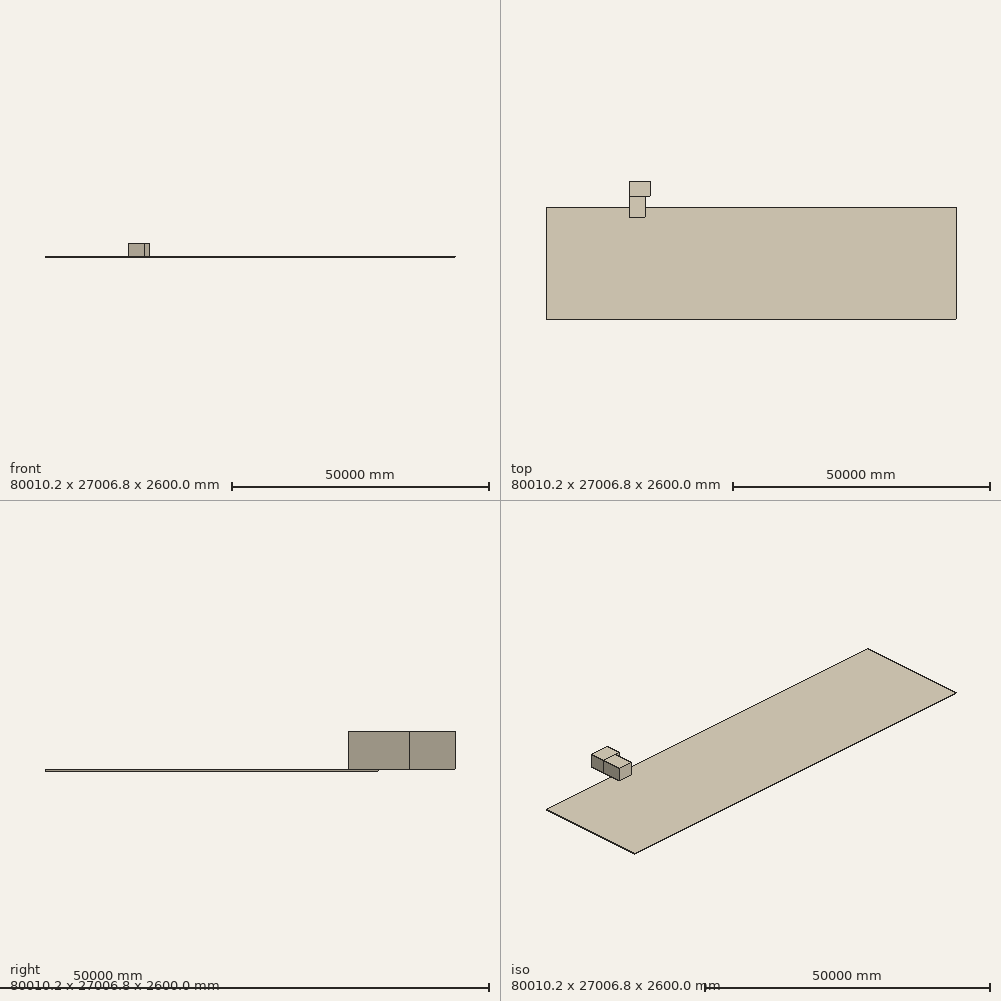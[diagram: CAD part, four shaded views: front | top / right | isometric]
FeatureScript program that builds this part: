
annotation { "Feature Type Name" : "Feature", "Feature Type Description" : "" }
export const myFeature = defineFeature(function(context is Context, id is Id, definition is map)
    precondition{}
    {
        {
            var Q0;
            Q0=qCreatedBy(makeId("Top.planeOp"),FACE);
            var sketch = newSketch(context, id + "F0", { "sketchPlane" : qUnion([Q0])});
            skLineSegment(sketch, "E0.bottom", {"start": v(-72.67, -73.64) * mm, "end": v(79937.58, -73.64) * mm});
            skLineSegment(sketch, "E0.top", {"start": v(-72.67, -21994.04) * mm, "end": v(79937.58, -21994.04) * mm});
            skLineSegment(sketch, "E0.left", {"start": v(-72.67, -73.64) * mm, "end": v(-72.67, -21994.04) * mm});
            skLineSegment(sketch, "E0.right", {"start": v(79937.58, -73.64) * mm, "end": v(79937.58, -21994.04) * mm});
            skSolve(sketch);
        }
        {
            var Q0;
            Q0 = qSketchRegion(id + "F0", true);
            extrude(context, id + "F1", {"entities" : qUnion([Q0]), "depth" : 100 * mm});
        }
        {
            var Q0;
            Q0=makeQuery(id+"F1.opExtrude","CAP_FACE",FACE,{"disambiguationData":[OSD([sQuery(id+"F0.wireOp",EDGE,"E0.bottom"),sQuery(id+"F0.wireOp",EDGE,"E0.top"),sQuery(id+"F0.wireOp",EDGE,"E0.left"),sQuery(id+"F0.wireOp",EDGE,"E0.right")])],"isStart":false});
            var sketch = newSketch(context, id + "F2", { "sketchPlane" : qUnion([Q0])});
            skLineSegment(sketch, "E1.bottom", {"start": v(16143.83, 1984.38) * mm, "end": v(20149.11, 1984.38) * mm});
            skLineSegment(sketch, "E1.top", {"start": v(16143.83, 5012.76) * mm, "end": v(20149.11, 5012.76) * mm});
            skLineSegment(sketch, "E1.left", {"start": v(16143.83, 1984.38) * mm, "end": v(16143.83, 5012.76) * mm});
            skLineSegment(sketch, "E1.right", {"start": v(20149.11, 1984.38) * mm, "end": v(20149.11, 5012.76) * mm});
            skSolve(sketch);
        }
        {
            var Q0;
            Q0=makeQuery(id+"F2.imprint","IMPRINT",FACE,{"disambiguationData":[TD([[makeQuery(id+"F2.imprint","IMPRINT",EDGE,{"derivedFrom":sQuery(id+"F2.wireOp",EDGE,"E1.bottom")}),1.0]])]});
            extrude(context, id + "F3", {"entities" : qUnion([Q0]), "depth" : 2500 * mm});
        }
        {
            var Q0;
            Q0=makeQuery(id+"F3.opExtrude","SWEPT_BODY",BODY,{"disambiguationData":[OSD([sQuery(id+"F2.wireOp",EDGE,"E1.bottom"),sQuery(id+"F2.wireOp",EDGE,"E1.top"),sQuery(id+"F2.wireOp",EDGE,"E1.left"),sQuery(id+"F2.wireOp",EDGE,"E1.right")])]});
            var Q1;
            Q1=makeQuery(id+"F3.opExtrude","SWEPT_EDGE",EDGE,{"disambiguationData":[OSD([sQuery(id+"F2.wireOp",EDGE,"E1.bottom"),sQuery(id+"F2.wireOp",EDGE,"E1.left")])]});
            transform(context, id + "F4", {"entities" : qUnion([Q0]), "transformType" : TransformType.ROTATION, "transformAxis" : qUnion([Q1]), "angle" : 90 * degree, "makeCopy" : true});
        }
    });
